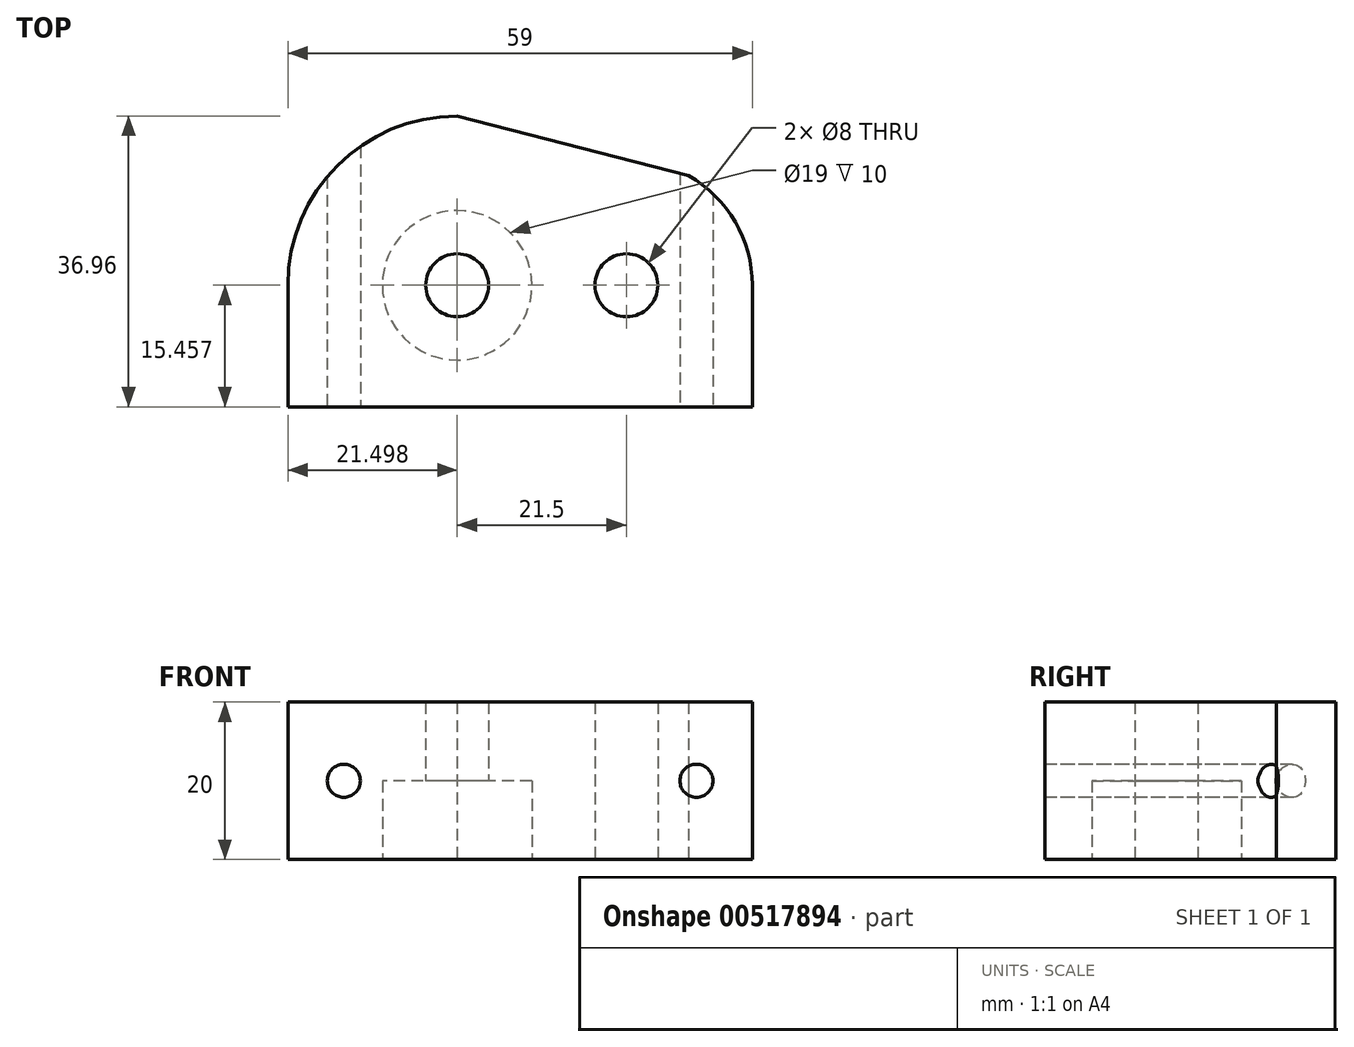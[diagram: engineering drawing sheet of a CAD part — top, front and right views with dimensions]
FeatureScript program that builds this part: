
annotation { "Feature Type Name" : "Feature", "Feature Type Description" : "" }
export const myFeature = defineFeature(function(context is Context, id is Id, definition is map)
    precondition{}
    {
        {
            var Q0;
            Q0=qCreatedBy(makeId("Top.planeOp"),FACE);
            var sketch = newSketch(context, id + "F0", { "sketchPlane" : qUnion([Q0])});
            skCircle(sketch, "E0", {"center": v(24.1, 15.46) * mm, "radius": 9.5 * mm});
            skCircle(sketch, "E1", {"center": v(45.6, 15.46) * mm, "radius": 4 * mm});
            skCircle(sketch, "E2", {"center": v(24.1, 15.46) * mm, "radius": 4 * mm});
            skLineSegment(sketch, "E3", {"start": v(2.6, 0) * mm, "end": v(2.6, 15.46) * mm});
            skLineSegment(sketch, "E4", {"start": v(61.6, 0) * mm, "end": v(61.6, 15.46) * mm});
            skLineSegment(sketch, "E5", {"start": v(2.6, 0) * mm, "end": v(61.6, 0) * mm});
            skArc(sketch, "E6", {"start": v(2.6, 15.46) * mm, "mid": v(8.9, 30.66) * mm, "end": v(24.1, 36.96) * mm});
            skArc(sketch, "E7", {"start": v(61.6, 15.46) * mm, "mid": v(59.42, 23.5) * mm, "end": v(53.5, 29.37) * mm});
            skLineSegment(sketch, "E8", {"start": v(53.5, 29.37) * mm, "end": v(24.1, 36.96) * mm});
            skSolve(sketch);
        }
        {
            var Q0;
            Q0=makeQuery(id+"F0.imprint","IMPRINT",FACE,{"disambiguationData":[TD([[makeQuery(id+"F0.imprint","IMPRINT",EDGE,{"derivedFrom":sQuery(id+"F0.wireOp",EDGE,"E0")}),-1.0]])]});
            var Q1;
            Q1=makeQuery(id+"F0.imprint","IMPRINT",FACE,{"disambiguationData":[TD([[makeQuery(id+"F0.imprint","IMPRINT",EDGE,{"derivedFrom":sQuery(id+"F0.wireOp",EDGE,"E0")}),1.0]])]});
            extrude(context, id + "F1", {"entities" : qUnion([Q0, Q1]), "depth" : 20 * mm, "offsetDistance" : 25 * mm});
        }
        {
            var Q0;
            Q0=makeQuery(id+"F0.imprint","IMPRINT",FACE,{"disambiguationData":[TD([[makeQuery(id+"F0.imprint","IMPRINT",EDGE,{"derivedFrom":sQuery(id+"F0.wireOp",EDGE,"E0")}),1.0]])]});
            var Q1;
            Q1=sQuery(id+"F0.wireOp",EDGE,"E0");
            extrude(context, id + "F2", {"entities" : qUnion([Q0]), "operationType" : NewBodyOperationType.REMOVE, "surfaceEntities" : qUnion([Q1]), "depth" : 10 * mm, "offsetDistance" : 25 * mm, "hasSecondDirection" : true, "secondDirectionOppositeDirection" : true, "secondDirectionDepth" : 25 * mm});
        }
        {
            var Q0;
            Q0=makeQuery(id+"F1.opExtrude","SWEPT_FACE",FACE,{"disambiguationData":[OSD([sQuery(id+"F0.wireOp",EDGE,"E5")])]});
            var sketch = newSketch(context, id + "F3", { "sketchPlane" : qUnion([Q0])});
            skCircle(sketch, "E9", {"center": v(54.5, 10) * mm, "radius": 2.1 * mm});
            skCircle(sketch, "E10", {"center": v(9.7, 10) * mm, "radius": 2.1 * mm});
            skSolve(sketch);
        }
        {
            var Q0;
            Q0=makeQuery(id+"F3.imprint","IMPRINT",FACE,{"disambiguationData":[TD([[makeQuery(id+"F3.imprint","IMPRINT",EDGE,{"derivedFrom":sQuery(id+"F3.wireOp",EDGE,"E9")}),1.0]])]});
            var Q1;
            Q1=makeQuery(id+"F3.imprint","IMPRINT",FACE,{"disambiguationData":[TD([[makeQuery(id+"F3.imprint","IMPRINT",EDGE,{"derivedFrom":sQuery(id+"F3.wireOp",EDGE,"E10")}),1.0]])]});
            var Q2;
            Q2=sQuery(id+"F3.wireOp",EDGE,"E9");
            var Q3;
            Q3=sQuery(id+"F3.wireOp",EDGE,"E10");
            extrude(context, id + "F4", {"entities" : qUnion([Q0, Q1]), "surfaceEntities" : qUnion([Q2, Q3]), "endBound" : BoundingType.UP_TO_NEXT, "oppositeDirection" : true, "depth" : 77 * mm, "offsetDistance" : 25 * mm});
        }
    });
